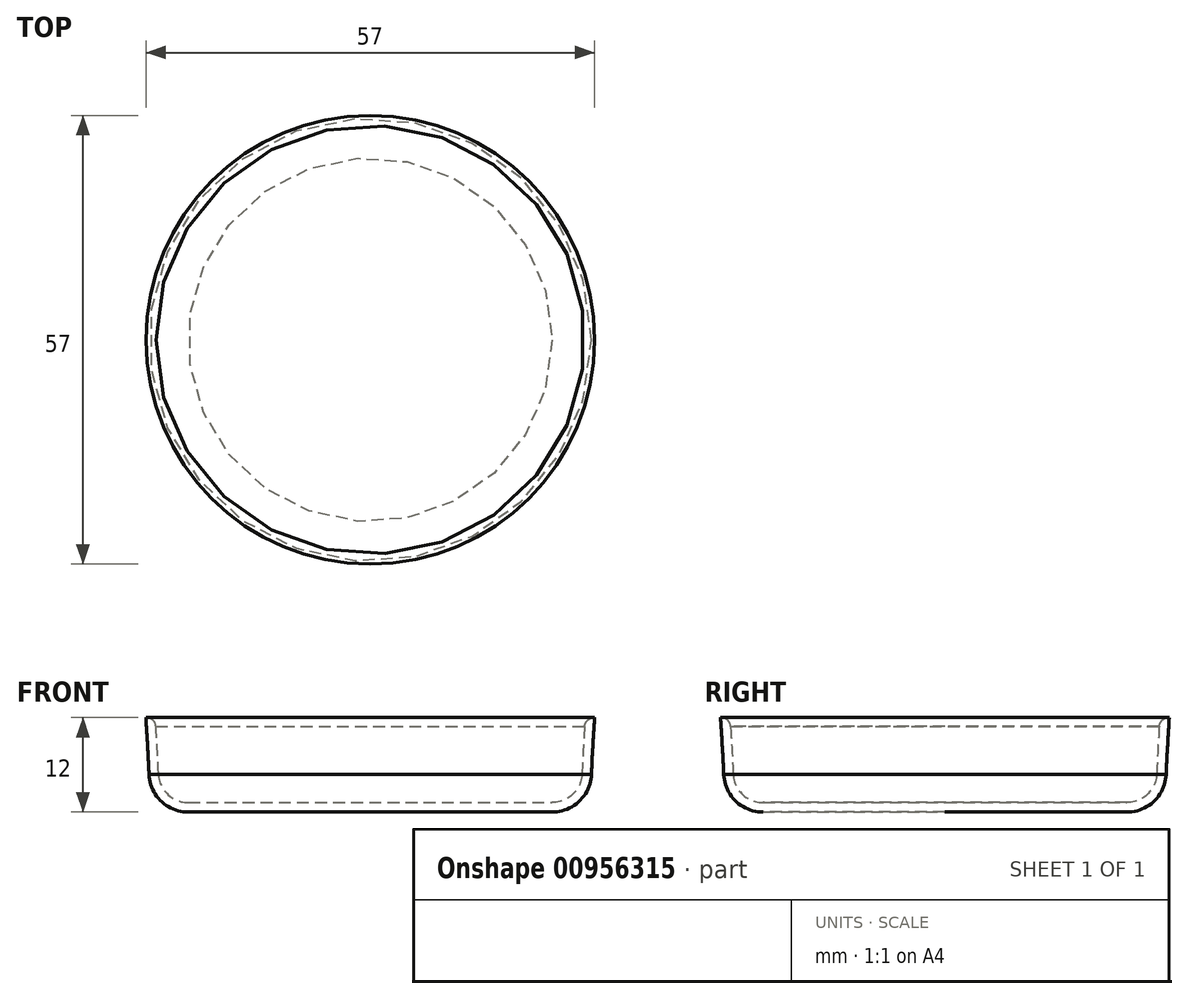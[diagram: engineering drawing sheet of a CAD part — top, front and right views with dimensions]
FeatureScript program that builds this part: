
annotation { "Feature Type Name" : "Feature", "Feature Type Description" : "" }
export const myFeature = defineFeature(function(context is Context, id is Id, definition is map)
    precondition{}
    {
        {
            var Q0;
            Q0=qCreatedBy(makeId("Top.planeOp"),FACE);
            var sketch = newSketch(context, id + "F0", { "sketchPlane" : qUnion([Q0])});
            skCircle(sketch, "E0", {"center": v(0, 0) * mm, "radius": 28 * mm});
            skSolve(sketch);
        }
        {
            var Q0;
            Q0=qCreatedBy(makeId("Top.planeOp"),FACE);
            cPlane(context, id + "F1", {"entities" : qUnion([Q0]), "cplaneType" : CPlaneType.OFFSET, "offset" : 12 * mm, "width" : 150 * mm, "height" : 150 * mm});
        }
        {
            var Q0;
            Q0=qCreatedBy(id+"F1.planeOp",FACE);
            var sketch = newSketch(context, id + "F2", { "sketchPlane" : qUnion([Q0])});
            skCircle(sketch, "E1", {"center": v(0, 0) * mm, "radius": 28.5 * mm});
            skSolve(sketch);
        }
        {
            var Q0;
            Q0=makeQuery(id+"F0.imprint","IMPRINT",FACE,{"disambiguationData":[TD([[makeQuery(id+"F0.imprint","IMPRINT",EDGE,{"derivedFrom":sQuery(id+"F0.wireOp",EDGE,"E0")}),1.0]])]});
            var Q1;
            Q1=makeQuery(id+"F2.imprint","IMPRINT",FACE,{"disambiguationData":[TD([[makeQuery(id+"F2.imprint","IMPRINT",EDGE,{"derivedFrom":sQuery(id+"F2.wireOp",EDGE,"E1")}),1.0]])]});
            loft(context, id + "F3", {"startCondition" : LoftEndDerivativeType.NORMAL_TO_PROFILE, "startMagnitude" : 1, "sheetProfilesArray" : [{ "sheetProfileEntities" : qUnion([Q0]) }, { "sheetProfileEntities" : qUnion([Q1]) }]});
        }
        {
            var Q0;
            Q0=makeQuery(id+"F3.opLoft","CAP_FACE",FACE,{"disambiguationData":[OSD([makeQuery(id+"F0.imprint","IMPRINT",FACE,{"disambiguationData":[TD([[makeQuery(id+"F0.imprint","IMPRINT",EDGE,{"derivedFrom":sQuery(id+"F0.wireOp",EDGE,"E0")}),1.0]])]})])],"isStart":true});
            fillet(context, id + "F4", {"entities" : qUnion([Q0]), "radius" : 5 * mm, "allowEdgeOverflow" : false});
        }
        {
            var Q0;
            Q0=makeQuery(id+"F3.opLoft","CAP_FACE",FACE,{"disambiguationData":[OSD([makeQuery(id+"F2.imprint","IMPRINT",FACE,{"disambiguationData":[TD([[makeQuery(id+"F2.imprint","IMPRINT",EDGE,{"derivedFrom":sQuery(id+"F2.wireOp",EDGE,"E1")}),1.0]])]})])],"isStart":true});
            shell(context, id + "F5", {"entities" : qUnion([Q0]), "thickness" : 1.2 * mm});
        }
        {
            var Q0;
            Q0=makeQuery(id+"F5.opShell","OFFSET_EDGE",EDGE,{"disambiguationData":[OSD([sQuery(id+"F2.wireOp",EDGE,"E1")])]});
            fillet(context, id + "F6", {"entities" : qUnion([Q0]), "radius" : 1.2 * mm, "tangentPropagation" : true, "allowEdgeOverflow" : false});
        }
    });
